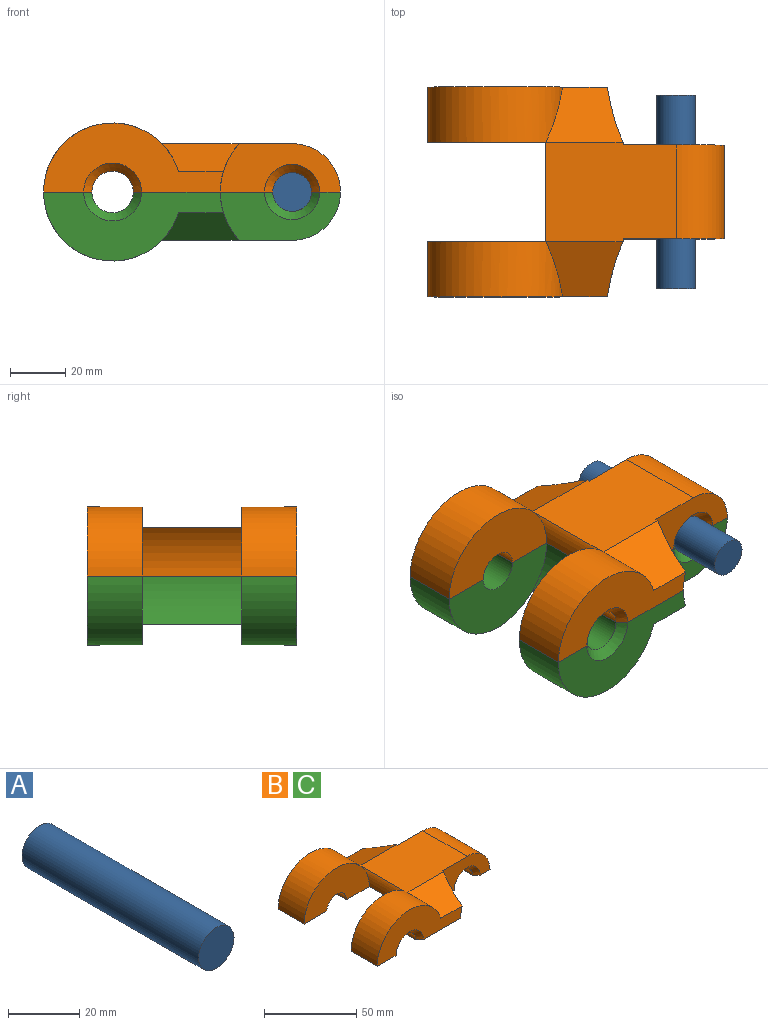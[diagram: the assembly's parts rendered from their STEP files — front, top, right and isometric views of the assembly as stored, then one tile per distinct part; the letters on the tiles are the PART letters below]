
ASSEMBLY  parts=3 mates=1
PART A: 3 faces, bbox 14x70x14 mm
  f0: cylinder r=7mm len=70mm, axis (0,-1,0), area 3078.8mm2, adj f1,f2
  f1: plane 14x14mm, normal (0,1,0), area 153.9mm2, adj f0
  f2: plane 14x14mm, normal (0,-1,0), area 153.9mm2, adj f0
PART B: 26 faces, bbox 107.5x76x25 mm
  f0: plane 50x25mm, normal (0,1,0), area 893.4mm2, adj f1,f3,f6,f23,f25
  f1: cylinder r=25mm len=48.85mm, axis (0,1,0), area 1306.3mm2, adj f0,f5,f12,f25
  f2: cylinder r=26mm len=21mm, axis (0,1,0), area 282.4mm2, adj f4,f5,f7,f12,f23
  f3: cylinder r=7.5mm len=17mm, axis (0,1,0), area 400.6mm2, adj f0,f11,f23,f25
  f4: plane 47.15x36mm, normal (0,0,1), area 1658.8mm2, adj f2,f6,f7,f8,f12,f15,f18,f21
  f5: plane 65.11x25mm, normal (0,-1,0), area 919.2mm2, adj f1,f2,f11,f12,f23,f25
  f6: cylinder r=25mm len=36mm, axis (0,-1,0), area 697.9mm2, adj f0,f4,f13,f23
  f7: plane 43.5x17.5mm, normal (0,-1,0), area 501.3mm2, adj f2,f4,f8,f10,f23,f24
  f8: cylinder r=17.5mm len=34mm, axis (0,-1,0), area 934.6mm2, adj f4,f7,f18,f24
  f9: cylinder r=7mm len=28mm, axis (0,-1,0), area 615.8mm2, adj f10,f19,f23,f24
  f10: cone r=7mm half-angle=45deg, axis (0,-1,0), area 113.3mm2, adj f7,f9,f23,f24
  f11: cone r=7.5mm half-angle=45deg, axis (0,-1,0), area 120mm2, adj f3,f5,f23,f25
  f12: plane 27.92x20mm, normal (0,-0.45,0.89), area 470.8mm2, adj f1,f2,f4,f5
  f13: plane 50x25mm, normal (0,-1,0), area 893.4mm2, adj f6,f14,f16,f22,f23
  f14: cylinder r=25mm len=48.85mm, axis (0,-1,0), area 1306.3mm2, adj f13,f17,f21,f22
  f15: cylinder r=26mm len=21mm, axis (0,-1,0), area 282.4mm2, adj f4,f17,f18,f21,f23
  f16: cylinder r=7.5mm len=17mm, axis (0,-1,0), area 400.6mm2, adj f13,f20,f22,f23
  f17: plane 65.11x25mm, normal (0,1,0), area 919.2mm2, adj f14,f15,f20,f21,f22,f23
  f18: plane 43.5x17.5mm, normal (0,1,0), area 501.3mm2, adj f4,f8,f15,f19,f23,f24
  f19: cone r=7mm half-angle=45deg, axis (0,1,0), area 113.3mm2, adj f9,f18,f23,f24
  f20: cone r=7.5mm half-angle=45deg, axis (0,1,0), area 120mm2, adj f16,f17,f22,f23
  f21: plane 27.92x20mm, normal (0,0.45,0.89), area 470.8mm2, adj f4,f14,f15,f17
  f22: plane 20x17.5mm, normal (0,0,-1), area 345.5mm2, adj f13,f14,f16,f17,f20
  f23: plane 76x50.5mm, normal (0,0,-1), area 2392mm2, adj f0,f2,f3,f5,f6,f7,f9,f10
  f24: plane 34x10.5mm, normal (0,0,-1), area 348mm2, adj f7,f8,f9,f10,f18,f19
  f25: plane 20x17.5mm, normal (0,0,-1), area 345.5mm2, adj f0,f1,f3,f5,f11
PART C: same geometry as B
PLACE A t=(107.86,-38.55,-11.94)mm
PLACE B t=(42.86,-38.55,-11.94)mm
PLACE C rot(axis=(1,0,0),180deg) t=(42.86,-2.55,-11.94)mm
MATE fastened A.f0 <-> C.f2  axis (0,-1,0) through (107.86,14.45,-11.94)mm
